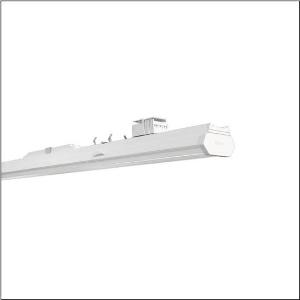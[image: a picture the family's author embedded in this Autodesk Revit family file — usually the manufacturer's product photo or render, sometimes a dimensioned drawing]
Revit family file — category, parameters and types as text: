
# Revit family: licross_r__11_protected_mo_51td1bdn68xg_8e9f
name_source: partatom
category: Lighting Fixtures
units: mm (PartAtom-declared; Revit-internal decimal feet)

## family parameters
Cut with Voids When Loaded = No
Host = Face
Light Source = No
Part Type = Normal
Room Calculation Point = No
Round Connector Dimension = Use Diameter
Shared = No

## types (1)
- --- (1 x LED, 8310 lm, 51.3 W, 6500K)
    Apparent Load = 51 VA
    CIE Flux Codes = 54 82 95 97 100
    Color Rendering = 80
    Color Temperature = 6500K
    Default Elevation = 1800 mm
    Description = Licross® 11 Protected MO, luminaire insert, of sheet steel, galvanised, coil coated, white, length: 1.500mm, width: 90mm, height: 101mm, LED rated luminous flux: 8.310lm, light colour: 865, SDCM (Standard Deviation of Colour Matching)MacAdam ≤ 2 SDCM (initial), control gear: DALI 2, with plug, 5-pole, with phase selection, mains connection: 220..240V, AC, 50/60Hz, rated input power: 51W, internal wiring halogen-free, primary optical cover: cover, of PMMA, light emission: direct distribution, primary light characteristic: symmetric, protection rating (complete): IP54, insulation class (complete): insulation class I (protective earthing), certification: CE, ENEC, VDE, UKCA, protection symbol: D if used in an environment with non-conductive dust loads with corresponding accessories, impact resistance: IK06, permissible ambient temperature for indoor applications: -25..+35°C, corresponds to IFS (International Featured Standards) requirements for safety and quality in the food industry, reducing of maximum allowable ambient temperature of 5°C with ceiling mounting, LABS conformity tested according to VDMA 24364:2018-05, packaging unit: 1 piece
    Height = 92 mm
    Lamp = 1 x LED
    Lamp Light Flux = 8310 lm
    Lamp Power = 51.3 W
    Lamp count = 1
    Length = 1500 mm
    Luminous efficacy = 162 lm/W
    Manufacturer = Siteco
    ModVariant = No
    Model = 51TD1BDN68XG
    Mounting Place = Ceiling
    Mounting Type = Pendant
    Number of Poles = 1
    OnlyDefault = Yes
    Power Factor = 1
    Product Name = Licross® 11 Protected MO
    Product group = luminaire insert | ceiling pendant
    ProductGroupID = 901
    Protection Class = Protection class I
    Protection Degree = IP 54
    RLX_Detail_Level = 1
    RLX_Emergency_Light_Flux = 0 lm
    RLX_Emergency_Type = 0
    RLX_Emergency_Type_DB = No
    RlxData = <blob elided: 24533 chars, md5=48afa47c>
    Socket = socket
    Standby Power = 0 W
    System Light Flux = 8310 lm
    System Power = 51 W
    Type Comments = factory setting: luminous flux: 100 % | dim-lin: 254 | 341 mA
    Type Image = l_1256145.jpg
    URL = http://relux.com
    VarID = @adj_058683
    Voltage = 0 V
    Weight = 0.00 kg
    Width = 88 mm

## geometry (parser evidence)
native form markers: Blend x4, Sweep x11
no freeform markers — native parametric forms only
